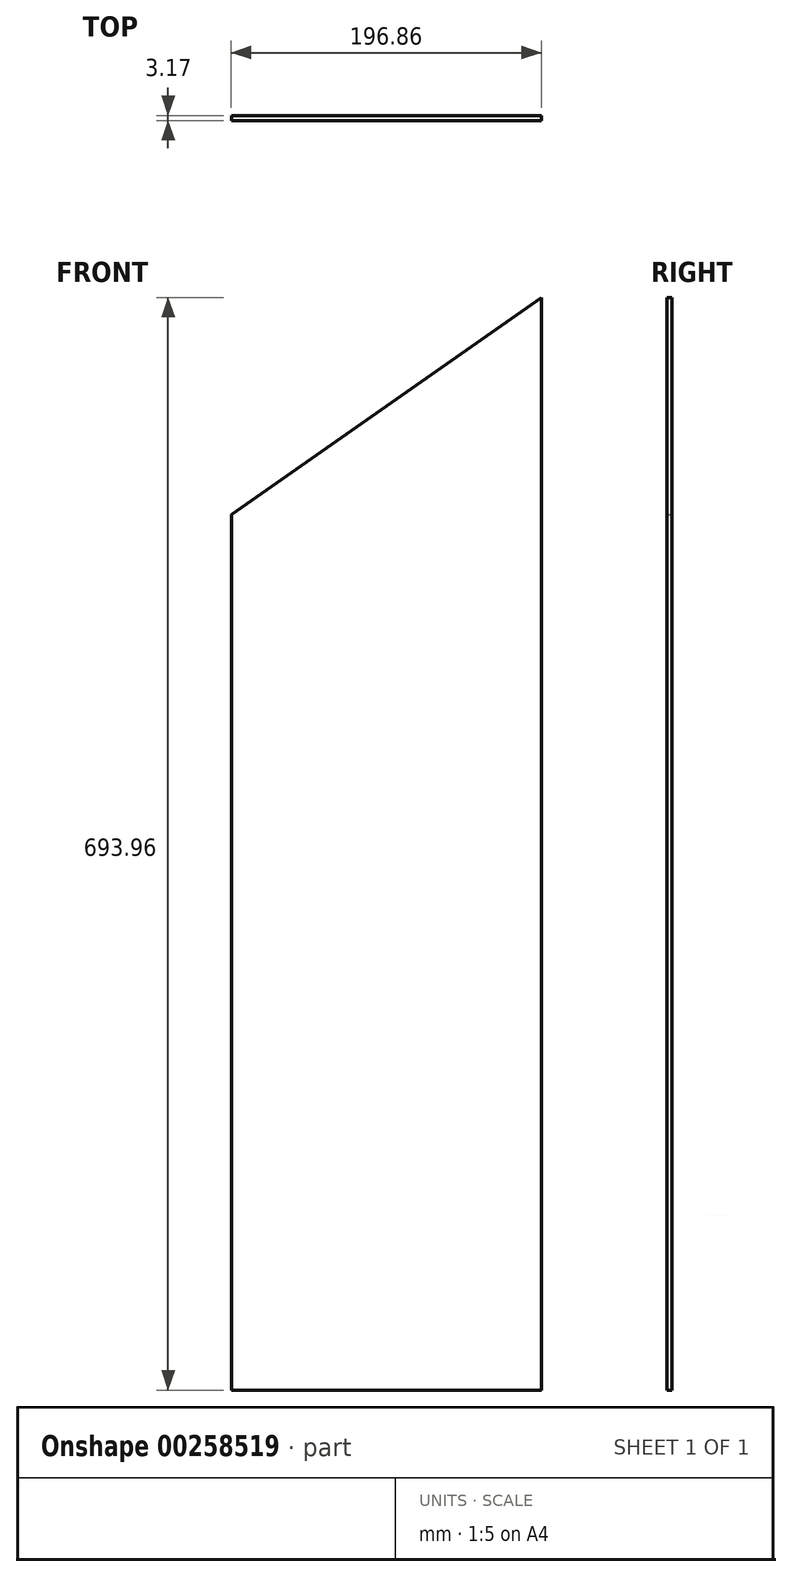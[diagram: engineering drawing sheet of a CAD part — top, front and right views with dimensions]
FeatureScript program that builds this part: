
annotation { "Feature Type Name" : "Feature", "Feature Type Description" : "" }
export const myFeature = defineFeature(function(context is Context, id is Id, definition is map)
    precondition{}
    {
        {
            var Q0;
            Q0=qCreatedBy(makeId("Front.planeOp"),FACE);
            var sketch = newSketch(context, id + "F0", { "sketchPlane" : qUnion([Q0])});
            skLineSegment(sketch, "E0.top", {"start": v(98.42, -346.98) * mm, "end": v(-98.43, -346.98) * mm});
            skLineSegment(sketch, "E0.left", {"start": v(98.43, 346.98) * mm, "end": v(98.43, -346.98) * mm});
            skLineSegment(sketch, "E0.right", {"start": v(-98.43, 209.15) * mm, "end": v(-98.43, -346.98) * mm});
            skPoint(sketch, "E0.middle", {"position": v(0, 0) * mm});
            skLineSegment(sketch, "E1", {"start": v(98.43, 346.98) * mm, "end": v(-98.43, 209.15) * mm});
            skPoint(sketch, "E2.orphan", {"position": v(-98.43, 346.98) * mm});
            skSolve(sketch);
        }
        {
            var Q0;
            Q0=makeQuery(id+"F0.imprint","IMPRINT",FACE,{"disambiguationData":[TD([[makeQuery(id+"F0.imprint","IMPRINT",EDGE,{"derivedFrom":sQuery(id+"F0.wireOp",EDGE,"E0.top")}),-1.0]])]});
            extrude(context, id + "F1", {"entities" : qUnion([Q0]), "depth" : 3.17 * mm});
        }
    });
